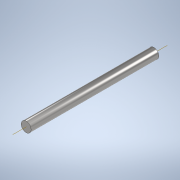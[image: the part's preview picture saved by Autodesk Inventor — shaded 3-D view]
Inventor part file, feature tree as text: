
AUTODESK INVENTOR PART (.ipt)
format: ipt  version: 2021.1 (Build 251245000, 245)  size: 96,256 bytes
history: native  units: in
note: dims shown in document units (in); Inventor stores cm internally (conversion verified against a paired STEP export)
features: extrude x1, sketch x1
ambient origin geometry x8: Origin, YZ Plane, XZ Plane, XY Plane, X Axis, Y Axis, Z Axis, Center Point
bodies: Solid1 (feature_tree)
feature tree (2):
  extrude  "Extrusion1"  Depth=8.0in TaperAngle=0.0deg
  sketch  "Sketch1"  dims[d0=0.625in d1=8.0in d2=0.0in]
